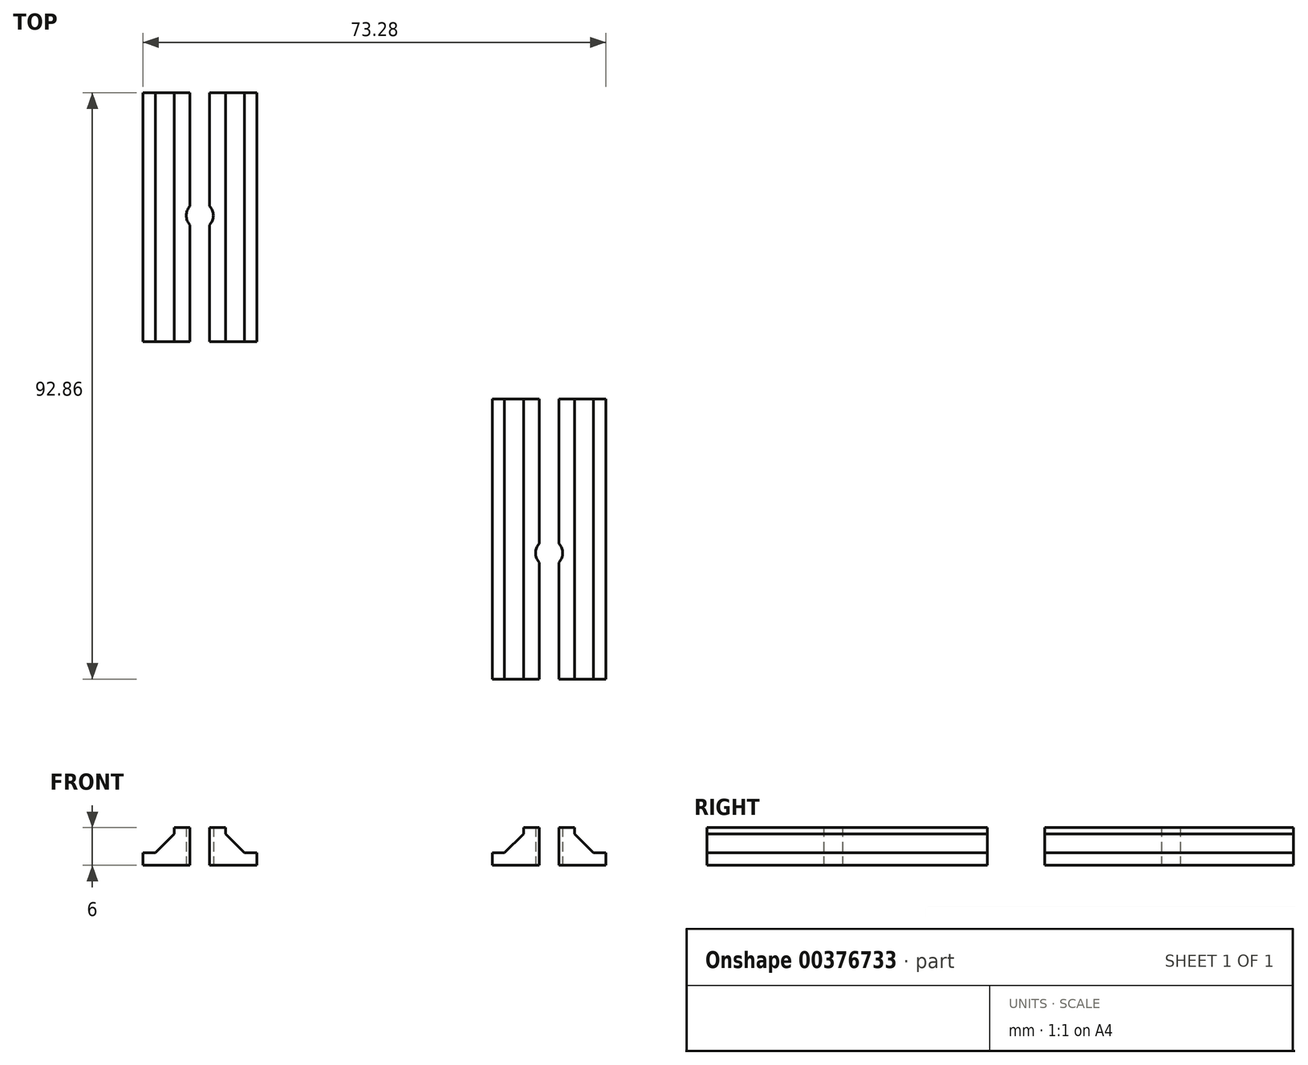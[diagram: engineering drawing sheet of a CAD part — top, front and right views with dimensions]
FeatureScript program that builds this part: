
annotation { "Feature Type Name" : "Feature", "Feature Type Description" : "" }
export const myFeature = defineFeature(function(context is Context, id is Id, definition is map)
    precondition{}
    {
        {
            var Q0;
            Q0=qCreatedBy(makeId("Top.planeOp"),FACE);
            var sketch = newSketch(context, id + "F0", { "sketchPlane" : qUnion([Q0])});
            skLineSegment(sketch, "E0.bottom", {"start": v(-18, 19.7) * mm, "end": v(0, 19.7) * mm});
            skLineSegment(sketch, "E0.top", {"start": v(-18, -19.7) * mm, "end": v(0, -19.7) * mm});
            skLineSegment(sketch, "E0.left", {"start": v(-18, 19.7) * mm, "end": v(-18, -19.7) * mm});
            skLineSegment(sketch, "E0.right", {"start": v(0, 19.7) * mm, "end": v(0, -19.7) * mm});
            skLineSegment(sketch, "E1.bottom", {"start": v(-13.05, 19.7) * mm, "end": v(-4.95, 19.7) * mm});
            skLineSegment(sketch, "E1.top", {"start": v(-13.05, -19.7) * mm, "end": v(-4.95, -19.7) * mm});
            skLineSegment(sketch, "E1.left", {"start": v(-13.05, 19.7) * mm, "end": v(-13.05, -19.7) * mm});
            skLineSegment(sketch, "E1.right", {"start": v(-4.95, 19.7) * mm, "end": v(-4.95, -19.7) * mm});
            skLineSegment(sketch, "E2.bottom", {"start": v(-10.55, 19.7) * mm, "end": v(-7.45, 19.7) * mm});
            skLineSegment(sketch, "E2.top", {"start": v(-10.55, -19.7) * mm, "end": v(-7.45, -19.7) * mm});
            skLineSegment(sketch, "E2.left", {"start": v(-10.55, 19.7) * mm, "end": v(-10.55, -19.7) * mm});
            skLineSegment(sketch, "E2.right", {"start": v(-7.45, 19.7) * mm, "end": v(-7.45, -19.7) * mm});
            skCircle(sketch, "E3", {"center": v(-9, 0.28) * mm, "radius": 2.15 * mm});
            skLineSegment(sketch, "E4.bottom", {"start": v(37.28, -28.76) * mm, "end": v(55.28, -28.76) * mm});
            skLineSegment(sketch, "E4.top", {"start": v(37.28, -73.16) * mm, "end": v(55.28, -73.16) * mm});
            skLineSegment(sketch, "E4.left", {"start": v(37.28, -28.76) * mm, "end": v(37.28, -73.16) * mm});
            skLineSegment(sketch, "E4.right", {"start": v(55.28, -28.76) * mm, "end": v(55.28, -73.16) * mm});
            skLineSegment(sketch, "E5.bottom", {"start": v(42.23, -28.76) * mm, "end": v(50.33, -28.76) * mm});
            skLineSegment(sketch, "E5.top", {"start": v(42.23, -73.16) * mm, "end": v(50.33, -73.16) * mm});
            skLineSegment(sketch, "E5.left", {"start": v(42.23, -28.76) * mm, "end": v(42.23, -73.16) * mm});
            skLineSegment(sketch, "E5.right", {"start": v(50.33, -28.76) * mm, "end": v(50.33, -73.16) * mm});
            skLineSegment(sketch, "E6.bottom", {"start": v(44.73, -28.76) * mm, "end": v(47.83, -28.76) * mm});
            skLineSegment(sketch, "E6.top", {"start": v(44.73, -73.16) * mm, "end": v(47.83, -73.16) * mm});
            skLineSegment(sketch, "E6.left", {"start": v(44.73, -28.76) * mm, "end": v(44.73, -73.16) * mm});
            skLineSegment(sketch, "E6.right", {"start": v(47.83, -28.76) * mm, "end": v(47.83, -73.16) * mm});
            skCircle(sketch, "E7", {"center": v(46.28, -53.18) * mm, "radius": 2.15 * mm});
            skSolve(sketch);
        }
        {
            var Q0;
            {var subQ0=sQuery(id+"F0.wireOp",EDGE,"E0.right");Q0=makeQuery(id+"F0.imprint","IMPRINT",FACE,{"disambiguationData":[TD([[makeQuery(id+"F0.imprint","IMPRINT",EDGE,{"derivedFrom":subQ0}),-1.0]])]});}
            var Q1;
            {var subQ0=sQuery(id+"F0.wireOp",EDGE,"E1.left");Q1=makeQuery(id+"F0.imprint","IMPRINT",FACE,{"disambiguationData":[TD([[makeQuery(id+"F0.imprint","IMPRINT",EDGE,{"derivedFrom":subQ0}),1.0]])]});}
            var Q2;
            {var subQ0=sQuery(id+"F0.wireOp",EDGE,"E1.right");Q2=makeQuery(id+"F0.imprint","IMPRINT",FACE,{"disambiguationData":[TD([[makeQuery(id+"F0.imprint","IMPRINT",EDGE,{"derivedFrom":subQ0}),-1.0]])]});}
            var Q3;
            Q3=makeQuery(id+"F0.imprint","IMPRINT",FACE,{"disambiguationData":[TD([[makeQuery(id+"F0.imprint","IMPRINT",EDGE,{"derivedFrom":sQuery(id+"F0.wireOp",EDGE,"E2.bottom")}),-1.0]])]});
            var Q4;
            {var subQ0=sQuery(id+"F0.wireOp",EDGE,"E0.left");Q4=makeQuery(id+"F0.imprint","IMPRINT",FACE,{"disambiguationData":[TD([[makeQuery(id+"F0.imprint","IMPRINT",EDGE,{"derivedFrom":subQ0}),1.0]])]});}
            var Q5;
            {var subQ0=sQuery(id+"F0.wireOp",EDGE,"E2.top");Q5=makeQuery(id+"F0.imprint","IMPRINT",FACE,{"disambiguationData":[TD([[makeQuery(id+"F0.imprint","IMPRINT",EDGE,{"derivedFrom":subQ0}),1.0]])]});}
            var Q6;
            {var subQ0=sQuery(id+"F0.wireOp",EDGE,"E4.left");Q6=makeQuery(id+"F0.imprint","IMPRINT",FACE,{"disambiguationData":[TD([[makeQuery(id+"F0.imprint","IMPRINT",EDGE,{"derivedFrom":subQ0}),1.0]])]});}
            var Q7;
            {var subQ5=sQuery(id+"F0.wireOp",EDGE,"E5.left");Q7=makeQuery(id+"F0.imprint","IMPRINT",FACE,{"disambiguationData":[TD([[makeQuery(id+"F0.imprint","IMPRINT",EDGE,{"derivedFrom":subQ5}),1.0]])]});}
            var Q8;
            {var subQ0=sQuery(id+"F0.wireOp",EDGE,"E6.bottom");Q8=makeQuery(id+"F0.imprint","IMPRINT",FACE,{"disambiguationData":[TD([[makeQuery(id+"F0.imprint","IMPRINT",EDGE,{"derivedFrom":subQ0}),-1.0]])]});}
            var Q9;
            {var subQ0=sQuery(id+"F0.wireOp",EDGE,"E5.right");Q9=makeQuery(id+"F0.imprint","IMPRINT",FACE,{"disambiguationData":[TD([[makeQuery(id+"F0.imprint","IMPRINT",EDGE,{"derivedFrom":subQ0}),-1.0]])]});}
            var Q10;
            {var subQ0=sQuery(id+"F0.wireOp",EDGE,"E4.right");Q10=makeQuery(id+"F0.imprint","IMPRINT",FACE,{"disambiguationData":[TD([[makeQuery(id+"F0.imprint","IMPRINT",EDGE,{"derivedFrom":subQ0}),-1.0]])]});}
            var Q11;
            {var subQ0=sQuery(id+"F0.wireOp",EDGE,"E6.top");Q11=makeQuery(id+"F0.imprint","IMPRINT",FACE,{"disambiguationData":[TD([[makeQuery(id+"F0.imprint","IMPRINT",EDGE,{"derivedFrom":subQ0}),1.0]])]});}
            extrude(context, id + "F1", {"entities" : qUnion([Q0, Q1, Q2, Q3, Q4, Q5, Q6, Q7, Q8, Q9, Q10, Q11]), "depth" : 2 * mm});
        }
        {
            var Q0;
            {var subQ0=sQuery(id+"F0.wireOp",EDGE,"E1.left");Q0=makeQuery(id+"F0.imprint","IMPRINT",FACE,{"disambiguationData":[TD([[makeQuery(id+"F0.imprint","IMPRINT",EDGE,{"derivedFrom":subQ0}),1.0]])]});}
            var Q1;
            {var subQ0=sQuery(id+"F0.wireOp",EDGE,"E1.right");Q1=makeQuery(id+"F0.imprint","IMPRINT",FACE,{"disambiguationData":[TD([[makeQuery(id+"F0.imprint","IMPRINT",EDGE,{"derivedFrom":subQ0}),-1.0]])]});}
            var Q2;
            {var subQ5=sQuery(id+"F0.wireOp",EDGE,"E5.left");Q2=makeQuery(id+"F0.imprint","IMPRINT",FACE,{"disambiguationData":[TD([[makeQuery(id+"F0.imprint","IMPRINT",EDGE,{"derivedFrom":subQ5}),1.0]])]});}
            var Q3;
            {var subQ0=sQuery(id+"F0.wireOp",EDGE,"E5.right");Q3=makeQuery(id+"F0.imprint","IMPRINT",FACE,{"disambiguationData":[TD([[makeQuery(id+"F0.imprint","IMPRINT",EDGE,{"derivedFrom":subQ0}),-1.0]])]});}
            extrude(context, id + "F2", {"entities" : qUnion([Q0, Q1, Q2, Q3]), "operationType" : NewBodyOperationType.ADD, "depth" : 6 * mm});
        }
        {
            var Q0;
            Q0=makeQuery(id+"F2.boolean.opBoolean","INTERSECT",EDGE,{"derivedFrom":[makeQuery(id+"F1.opExtrude","CAP_FACE",FACE,{"disambiguationData":[OSD([sQuery(id+"F0.wireOp",EDGE,"E0.bottom"),sQuery(id+"F0.wireOp",EDGE,"E0.top"),sQuery(id+"F0.wireOp",EDGE,"E0.left"),sQuery(id+"F0.wireOp",EDGE,"E0.right"),sQuery(id+"F0.wireOp",EDGE,"E1.bottom"),sQuery(id+"F0.wireOp",EDGE,"E1.top"),sQuery(id+"F0.wireOp",EDGE,"E2.bottom"),sQuery(id+"F0.wireOp",EDGE,"E2.top")])],"isStart":false}),makeQuery(id+"F2.opExtrude","SWEPT_FACE",FACE,{"disambiguationData":[OSD([sQuery(id+"F0.wireOp",EDGE,"E1.left")])]})]});
            var Q1;
            Q1=makeQuery(id+"F2.boolean.opBoolean","INTERSECT",EDGE,{"derivedFrom":[makeQuery(id+"F1.opExtrude","CAP_FACE",FACE,{"disambiguationData":[OSD([sQuery(id+"F0.wireOp",EDGE,"E0.bottom"),sQuery(id+"F0.wireOp",EDGE,"E0.top"),sQuery(id+"F0.wireOp",EDGE,"E0.left"),sQuery(id+"F0.wireOp",EDGE,"E0.right"),sQuery(id+"F0.wireOp",EDGE,"E1.bottom"),sQuery(id+"F0.wireOp",EDGE,"E1.top"),sQuery(id+"F0.wireOp",EDGE,"E2.bottom"),sQuery(id+"F0.wireOp",EDGE,"E2.top")])],"isStart":false}),makeQuery(id+"F2.opExtrude","SWEPT_FACE",FACE,{"disambiguationData":[OSD([sQuery(id+"F0.wireOp",EDGE,"E1.right")])]})]});
            var Q2;
            Q2=makeQuery(id+"F2.boolean.opBoolean","INTERSECT",EDGE,{"derivedFrom":[makeQuery(id+"F1.opExtrude","CAP_FACE",FACE,{"disambiguationData":[OSD([sQuery(id+"F0.wireOp",EDGE,"E4.bottom"),sQuery(id+"F0.wireOp",EDGE,"E4.top"),sQuery(id+"F0.wireOp",EDGE,"E4.left"),sQuery(id+"F0.wireOp",EDGE,"E4.right"),sQuery(id+"F0.wireOp",EDGE,"E5.bottom"),sQuery(id+"F0.wireOp",EDGE,"E5.top"),sQuery(id+"F0.wireOp",EDGE,"E6.bottom"),sQuery(id+"F0.wireOp",EDGE,"E6.top"),sQuery(id+"F0.wireOp",EDGE,"E7")])],"isStart":false}),makeQuery(id+"F2.opExtrude","SWEPT_FACE",FACE,{"disambiguationData":[OSD([sQuery(id+"F0.wireOp",EDGE,"E5.left")])]})]});
            var Q3;
            Q3=makeQuery(id+"F2.boolean.opBoolean","INTERSECT",EDGE,{"derivedFrom":[makeQuery(id+"F1.opExtrude","CAP_FACE",FACE,{"disambiguationData":[OSD([sQuery(id+"F0.wireOp",EDGE,"E4.bottom"),sQuery(id+"F0.wireOp",EDGE,"E4.top"),sQuery(id+"F0.wireOp",EDGE,"E4.left"),sQuery(id+"F0.wireOp",EDGE,"E4.right"),sQuery(id+"F0.wireOp",EDGE,"E5.bottom"),sQuery(id+"F0.wireOp",EDGE,"E5.top"),sQuery(id+"F0.wireOp",EDGE,"E6.bottom"),sQuery(id+"F0.wireOp",EDGE,"E6.top"),sQuery(id+"F0.wireOp",EDGE,"E7")])],"isStart":false}),makeQuery(id+"F2.opExtrude","SWEPT_FACE",FACE,{"disambiguationData":[OSD([sQuery(id+"F0.wireOp",EDGE,"E5.right")])]})]});
            chamfer(context, id + "F3", {"entities" : qUnion([Q0, Q1, Q2, Q3]), "width" : 3 * mm, "tangentPropagation" : true});
        }
    });
